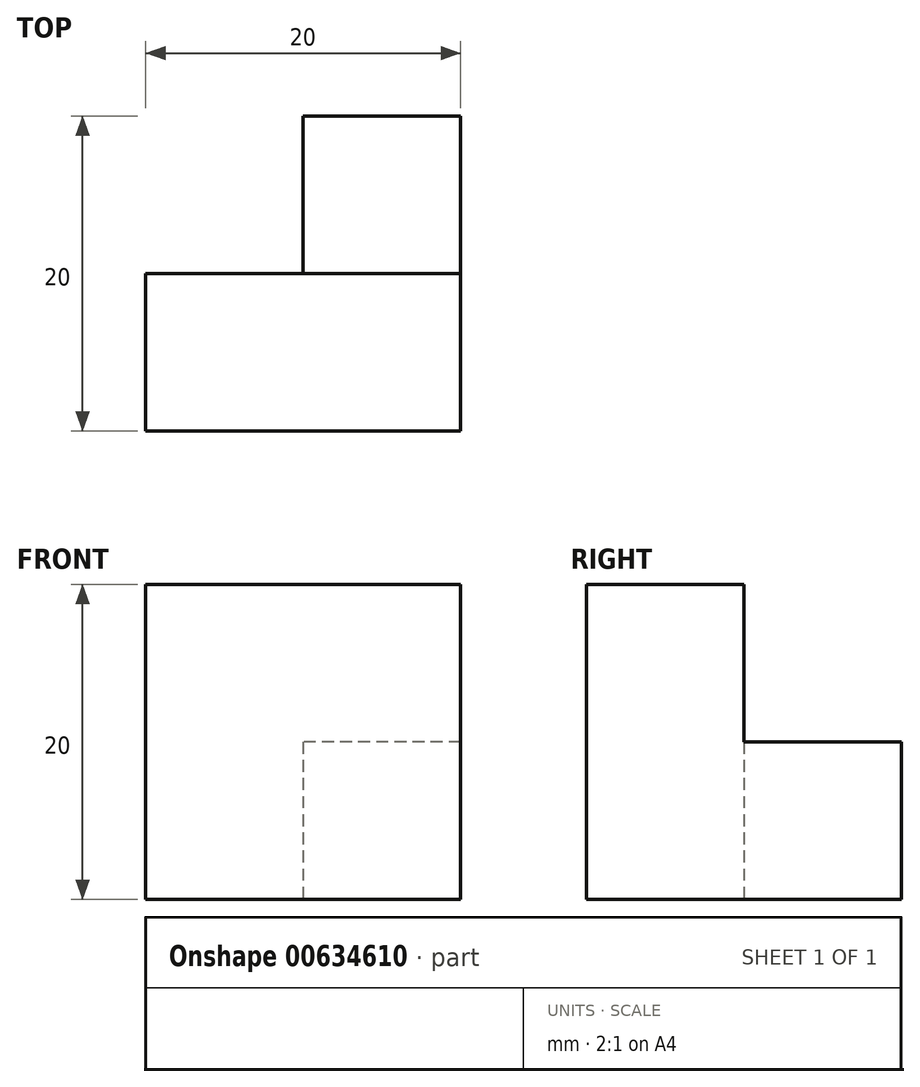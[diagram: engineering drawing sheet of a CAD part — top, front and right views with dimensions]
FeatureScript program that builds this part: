
annotation { "Feature Type Name" : "Feature", "Feature Type Description" : "" }
export const myFeature = defineFeature(function(context is Context, id is Id, definition is map)
    precondition{}
    {
        {
            var Q0;
            Q0=qCreatedBy(makeId("Top.planeOp"),FACE);
            var sketch = newSketch(context, id + "F0", { "sketchPlane" : qUnion([Q0]), "disableImprinting" : false});
            skLineSegment(sketch, "E0.bottom", {"start": v(0, 0) * mm, "end": v(-20, 0) * mm});
            skLineSegment(sketch, "E0.top", {"start": v(0, 10) * mm, "end": v(-20, 10) * mm});
            skLineSegment(sketch, "E0.left", {"start": v(0, 0) * mm, "end": v(0, 10) * mm});
            skLineSegment(sketch, "E0.right", {"start": v(-20, 0) * mm, "end": v(-20, 10) * mm});
            skPoint(sketch, "E1.oppositeSnap0", {"position": v(-10, 10) * mm});
            skLineSegment(sketch, "E1.bottom", {"start": v(0, 0) * mm, "end": v(-10, 0) * mm});
            skLineSegment(sketch, "E1.top", {"start": v(0, 20) * mm, "end": v(-10, 20) * mm});
            skLineSegment(sketch, "E1.left", {"start": v(0, 0) * mm, "end": v(0, 20) * mm});
            skLineSegment(sketch, "E1.right", {"start": v(-10, 0) * mm, "end": v(-10, 20) * mm});
            skSolve(sketch);
        }
        {
            var Q0;
            {var subQ0=sQuery(id+"F0.wireOp",EDGE,"E0.bottom");Q0=makeQuery(id+"F0.imprint","IMPRINT",FACE,{"disambiguationData":[TD([[makeQuery(id+"F0.imprint","IMPRINT",EDGE,{"derivedFrom":subQ0}),-1.0]])]});}
            extrude(context, id + "F1", {"entities" : qUnion([Q0]), "depth" : 20 * mm, "offsetDistance" : 25 * mm});
        }
        {
            var Q0;
            {var subQ5=sQuery(id+"F0.wireOp",EDGE,"E1.top");Q0=makeQuery(id+"F0.imprint","IMPRINT",FACE,{"disambiguationData":[TD([[makeQuery(id+"F0.imprint","IMPRINT",EDGE,{"derivedFrom":subQ5}),1.0]])]});}
            var Q1;
            {var subQ5=sQuery(id+"F0.wireOp",EDGE,"E1.bottom");Q1=makeQuery(id+"F0.imprint","IMPRINT",FACE,{"disambiguationData":[TD([[makeQuery(id+"F0.imprint","IMPRINT",EDGE,{"derivedFrom":subQ5}),-1.0]])]});}
            extrude(context, id + "F2", {"entities" : qUnion([Q0, Q1]), "operationType" : NewBodyOperationType.ADD, "depth" : 10 * mm, "offsetDistance" : 25 * mm});
        }
    });
